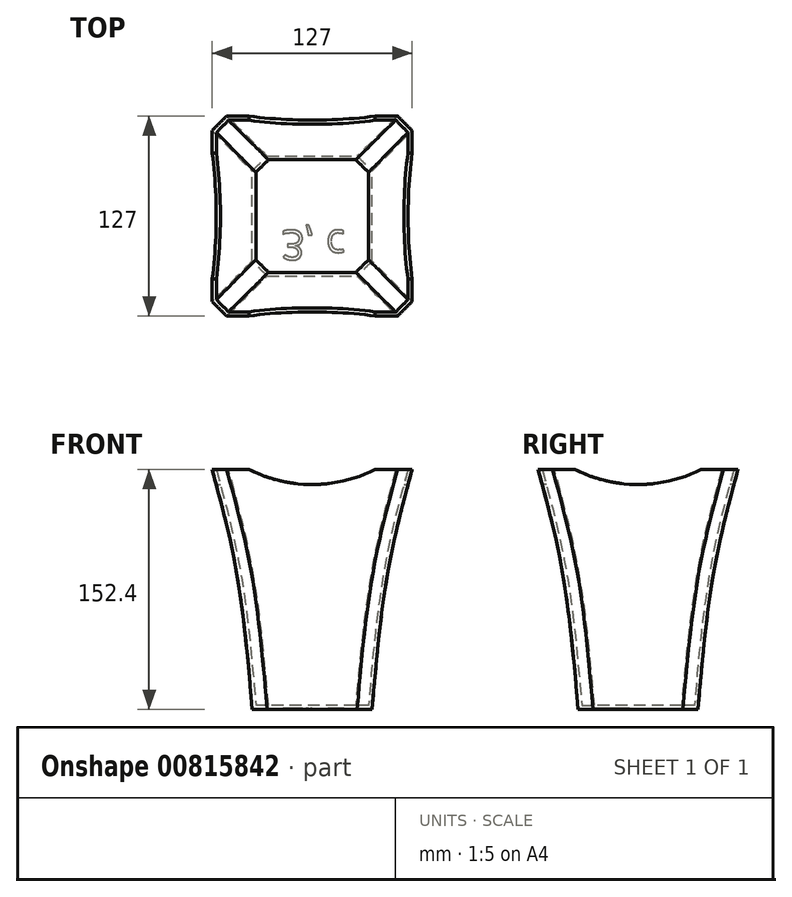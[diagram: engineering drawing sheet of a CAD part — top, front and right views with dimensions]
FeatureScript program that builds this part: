
annotation { "Feature Type Name" : "Feature", "Feature Type Description" : "" }
export const myFeature = defineFeature(function(context is Context, id is Id, definition is map)
    precondition{}
    {
        {
            var Q0;
            Q0=qCreatedBy(makeId("Top.planeOp"),FACE);
            var sketch = newSketch(context, id + "F0", { "sketchPlane" : qUnion([Q0])});
            skLineSegment(sketch, "E0.bottom", {"start": v(-38.1, -38.1) * mm, "end": v(38.1, -38.1) * mm});
            skLineSegment(sketch, "E0.top", {"start": v(-38.1, 38.1) * mm, "end": v(38.1, 38.1) * mm});
            skLineSegment(sketch, "E0.left", {"start": v(-38.1, -38.1) * mm, "end": v(-38.1, 38.1) * mm});
            skLineSegment(sketch, "E0.right", {"start": v(38.1, -38.1) * mm, "end": v(38.1, 38.1) * mm});
            skPoint(sketch, "E0.middle", {"position": v(0, 0) * mm});
            skSolve(sketch);
        }
        {
            var Q0;
            Q0=qCreatedBy(makeId("Top.planeOp"),FACE);
            cPlane(context, id + "F1", {"entities" : qUnion([Q0]), "cplaneType" : CPlaneType.OFFSET, "offset" : 101.6 * mm, "width" : 152.4 * mm, "height" : 152.4 * mm});
        }
        {
            var Q0;
            Q0=qCreatedBy(id+"F1.planeOp",FACE);
            var sketch = newSketch(context, id + "F2", { "sketchPlane" : qUnion([Q0])});
            skLineSegment(sketch, "E1.bottom", {"start": v(-50.8, 50.8) * mm, "end": v(50.8, 50.8) * mm});
            skLineSegment(sketch, "E1.top", {"start": v(-50.8, -50.8) * mm, "end": v(50.8, -50.8) * mm});
            skLineSegment(sketch, "E1.left", {"start": v(-50.8, 50.8) * mm, "end": v(-50.8, -50.8) * mm});
            skLineSegment(sketch, "E1.right", {"start": v(50.8, 50.8) * mm, "end": v(50.8, -50.8) * mm});
            skPoint(sketch, "E1.middle", {"position": v(0, 0) * mm});
            skSolve(sketch);
        }
        {
            var Q0;
            Q0=qCreatedBy(id+"F1.planeOp",FACE);
            cPlane(context, id + "F3", {"entities" : qUnion([Q0]), "cplaneType" : CPlaneType.OFFSET, "offset" : 50.8 * mm, "width" : 152.4 * mm, "height" : 152.4 * mm});
        }
        {
            var Q0;
            Q0=qCreatedBy(id+"F3.planeOp",FACE);
            var sketch = newSketch(context, id + "F4", { "sketchPlane" : qUnion([Q0])});
            skLineSegment(sketch, "E2.bottom", {"start": v(-63.5, -63.5) * mm, "end": v(63.5, -63.5) * mm});
            skLineSegment(sketch, "E2.top", {"start": v(-63.5, 63.5) * mm, "end": v(63.5, 63.5) * mm});
            skLineSegment(sketch, "E2.left", {"start": v(-63.5, -63.5) * mm, "end": v(-63.5, 63.5) * mm});
            skLineSegment(sketch, "E2.right", {"start": v(63.5, -63.5) * mm, "end": v(63.5, 63.5) * mm});
            skPoint(sketch, "E2.middle", {"position": v(0, 0) * mm});
            skSolve(sketch);
        }
        {
            var Q0;
            Q0=makeQuery(id+"F0.imprint","IMPRINT",FACE,{"disambiguationData":[TD([[makeQuery(id+"F0.imprint","IMPRINT",EDGE,{"derivedFrom":sQuery(id+"F0.wireOp",EDGE,"E0.bottom")}),1.0]])]});
            var Q1;
            Q1=makeQuery(id+"F2.imprint","IMPRINT",FACE,{"disambiguationData":[TD([[makeQuery(id+"F2.imprint","IMPRINT",EDGE,{"derivedFrom":sQuery(id+"F2.wireOp",EDGE,"E1.bottom")}),-1.0]])]});
            var Q2;
            Q2=makeQuery(id+"F4.imprint","IMPRINT",FACE,{"disambiguationData":[TD([[makeQuery(id+"F4.imprint","IMPRINT",EDGE,{"derivedFrom":sQuery(id+"F4.wireOp",EDGE,"E2.bottom")}),1.0]])]});
            loft(context, id + "F5", {"sheetProfilesArray" : [{ "sheetProfileEntities" : qUnion([Q0]) }, { "sheetProfileEntities" : qUnion([Q1]) }, { "sheetProfileEntities" : qUnion([Q2]) }]});
        }
        {
            var Q0;
            Q0=makeQuery(id+"F5.opLoft","SWEPT_EDGE",EDGE,{"disambiguationData":[OSD([sQuery(id+"F0.wireOp",EDGE,"E0.bottom"),sQuery(id+"F0.wireOp",EDGE,"E0.right"),sQuery(id+"F2.wireOp",EDGE,"E1.top"),sQuery(id+"F2.wireOp",EDGE,"E1.right")])]});
            var Q1;
            Q1=makeQuery(id+"F5.opLoft","SWEPT_EDGE",EDGE,{"disambiguationData":[OSD([sQuery(id+"F0.wireOp",EDGE,"E0.top"),sQuery(id+"F0.wireOp",EDGE,"E0.right"),sQuery(id+"F2.wireOp",EDGE,"E1.bottom"),sQuery(id+"F2.wireOp",EDGE,"E1.right")])]});
            var Q2;
            Q2=makeQuery(id+"F5.opLoft","SWEPT_EDGE",EDGE,{"disambiguationData":[OSD([sQuery(id+"F0.wireOp",EDGE,"E0.bottom"),sQuery(id+"F0.wireOp",EDGE,"E0.left"),sQuery(id+"F2.wireOp",EDGE,"E1.top"),sQuery(id+"F2.wireOp",EDGE,"E1.left")])]});
            var Q3;
            Q3=makeQuery(id+"F5.opLoft","SWEPT_EDGE",EDGE,{"disambiguationData":[OSD([sQuery(id+"F0.wireOp",EDGE,"E0.top"),sQuery(id+"F0.wireOp",EDGE,"E0.left"),sQuery(id+"F2.wireOp",EDGE,"E1.bottom"),sQuery(id+"F2.wireOp",EDGE,"E1.left")])]});
            chamfer(context, id + "F6", {"entities" : qUnion([Q0, Q1, Q2, Q3]), "width" : 9.52 * mm, "tangentPropagation" : true});
        }
        {
            var Q0;
            Q0=makeQuery(id+"F5.opLoft","CAP_FACE",FACE,{"disambiguationData":[OSD([makeQuery(id+"F4.imprint","IMPRINT",FACE,{"disambiguationData":[TD([[makeQuery(id+"F4.imprint","IMPRINT",EDGE,{"derivedFrom":sQuery(id+"F4.wireOp",EDGE,"E2.bottom")}),1.0]])]})])],"isStart":true});
            shell(context, id + "F7", {"entities" : qUnion([Q0]), "thickness" : 2.54 * mm});
        }
        {
            var Q0;
            Q0=qCreatedBy(makeId("Front.planeOp"),FACE);
            var sketch = newSketch(context, id + "F8", { "sketchPlane" : qUnion([Q0])});
            skArc(sketch, "E3", {"start": v(-40.04, 152.4) * mm, "mid": v(0, 142.88) * mm, "end": v(40.04, 152.4) * mm});
            skLineSegment(sketch, "E4", {"start": v(-40.04, 152.4) * mm, "end": v(40.04, 152.4) * mm});
            skLineSegment(sketch, "E5", {"start": v(74.8, 142.88) * mm, "end": v(-42.15, 142.88) * mm, "construction": true});
            skSolve(sketch);
        }
        {
            var Q0;
            Q0=makeQuery(id+"F8.imprint","IMPRINT",FACE,{"disambiguationData":[TD([[makeQuery(id+"F8.imprint","IMPRINT",EDGE,{"derivedFrom":sQuery(id+"F8.wireOp",EDGE,"E3")}),1.0]])]});
            extrude(context, id + "F9", {"entities" : qUnion([Q0]), "operationType" : NewBodyOperationType.REMOVE, "endBound" : BoundingType.THROUGH_ALL, "oppositeDirection" : true, "depth" : 25.4 * mm, "offsetDistance" : 25.4 * mm, "hasSecondDirection" : true, "secondDirectionBound" : SecondDirectionBoundingType.THROUGH_ALL, "secondDirectionOppositeDirection" : false, "secondDirectionDepth" : 25.4 * mm});
        }
        {
            var Q0;
            Q0=qCreatedBy(makeId("Right.planeOp"),FACE);
            var sketch = newSketch(context, id + "F10", { "sketchPlane" : qUnion([Q0])});
            skArc(sketch, "E6", {"start": v(-40.04, 152.4) * mm, "mid": v(0, 142.88) * mm, "end": v(40.04, 152.4) * mm});
            skLineSegment(sketch, "E7", {"start": v(-36.41, 142.88) * mm, "end": v(33.05, 142.88) * mm, "construction": true});
            skLineSegment(sketch, "E8", {"start": v(-40.04, 152.4) * mm, "end": v(40.04, 152.4) * mm});
            skSolve(sketch);
        }
        {
            var Q0;
            Q0=makeQuery(id+"F10.imprint","IMPRINT",FACE,{"disambiguationData":[TD([[makeQuery(id+"F10.imprint","IMPRINT",EDGE,{"derivedFrom":sQuery(id+"F10.wireOp",EDGE,"E6")}),1.0]])]});
            extrude(context, id + "F11", {"entities" : qUnion([Q0]), "operationType" : NewBodyOperationType.REMOVE, "endBound" : BoundingType.THROUGH_ALL, "oppositeDirection" : true, "depth" : 25.4 * mm, "offsetDistance" : 25.4 * mm, "hasSecondDirection" : true, "secondDirectionBound" : SecondDirectionBoundingType.THROUGH_ALL, "secondDirectionOppositeDirection" : false, "secondDirectionDepth" : 25.4 * mm});
        }
        {
            var Q0;
            Q0=makeQuery(id+"F5.opLoft","CAP_FACE",FACE,{"disambiguationData":[OSD([makeQuery(id+"F0.imprint","IMPRINT",FACE,{"disambiguationData":[TD([[makeQuery(id+"F0.imprint","IMPRINT",EDGE,{"derivedFrom":sQuery(id+"F0.wireOp",EDGE,"E0.bottom")}),1.0]])]})])],"isStart":true});
            var sketch = newSketch(context, id + "F12", { "sketchPlane" : qUnion([Q0])});
            skText(sketch, "E9", { "text": "3, c", "fontName": "OpenSans-Regular.ttf"});
            const initialGuessF12  = {"E9": [-0.0197, 0.00902, 1, 0, 0.01893]};
            skSetInitialGuess(sketch, initialGuessF12);
            skSolve(sketch);
        }
        {
            var Q0;
            Q0 = qSketchRegion(id + "F12", true);
            extrude(context, id + "F13", {"entities" : qUnion([Q0]), "operationType" : NewBodyOperationType.REMOVE, "oppositeDirection" : true, "depth" : 0.76 * mm, "offsetDistance" : 25.4 * mm});
        }
    });
